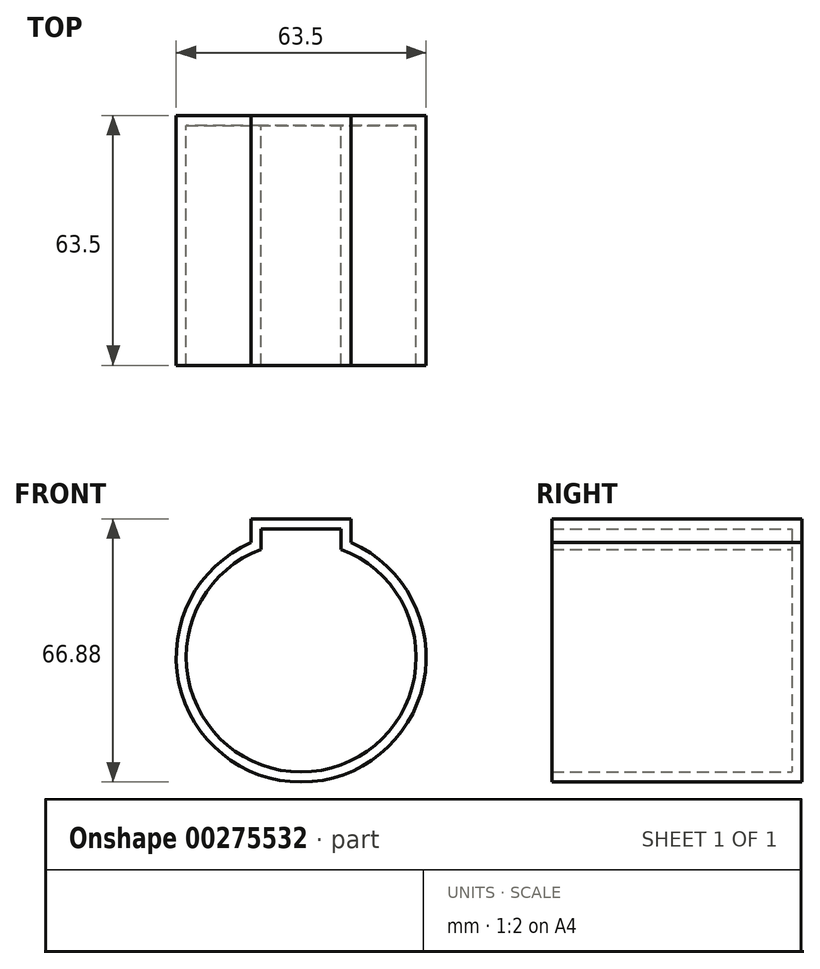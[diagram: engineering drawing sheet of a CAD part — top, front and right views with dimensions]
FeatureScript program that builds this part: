
annotation { "Feature Type Name" : "Feature", "Feature Type Description" : "" }
export const myFeature = defineFeature(function(context is Context, id is Id, definition is map)
    precondition{}
    {
        {
            var Q0;
            Q0=qCreatedBy(makeId("Front.planeOp"),FACE);
            var sketch = newSketch(context, id + "F0", { "sketchPlane" : qUnion([Q0])});
            skCircle(sketch, "E0", {"center": v(0, 0) * mm, "radius": 31.75 * mm});
            skLineSegment(sketch, "E1.bottom", {"start": v(12.7, 35.13) * mm, "end": v(-12.7, 35.13) * mm});
            skLineSegment(sketch, "E1.top", {"start": v(12.7, 28.37) * mm, "end": v(-12.7, 28.37) * mm});
            skLineSegment(sketch, "E1.left", {"start": v(12.7, 35.13) * mm, "end": v(12.7, 28.37) * mm});
            skLineSegment(sketch, "E1.right", {"start": v(-12.7, 35.13) * mm, "end": v(-12.7, 28.37) * mm});
            skPoint(sketch, "E1.middle", {"position": v(0, 31.75) * mm});
            skCircle(sketch, "E2", {"center": v(0, 0) * mm, "radius": 29.08 * mm});
            skSolve(sketch);
        }
        {
            var Q0;
            {var subQ5=sQuery(id+"F0.wireOp",EDGE,"E1.bottom");Q0=makeQuery(id+"F0.imprint","IMPRINT",FACE,{"disambiguationData":[TD([[makeQuery(id+"F0.imprint","IMPRINT",EDGE,{"derivedFrom":subQ5}),1.0]])]});}
            var Q1;
            {var subQ0=sQuery(id+"F0.wireOp",EDGE,"E1.left");var subQ3=sQuery(id+"F0.wireOp",EDGE,"E0");var subQ4=makeQuery(id+"F0.imprint","INTERSECT",VERTEX,{"derivedFrom":[subQ3,subQ0]});Q1=makeQuery(id+"F0.imprint","IMPRINT",FACE,{"disambiguationData":[TD([[makeQuery(id+"F0.imprint","IMPRINT",EDGE,{"disambiguationData":[TD([[subQ4,1.0]])],"derivedFrom":subQ3}),1.0]])]});}
            var Q2;
            {var subQ0=sQuery(id+"F0.wireOp",EDGE,"E2");var subQ1=sQuery(id+"F0.wireOp",EDGE,"E1.top");var subQ2=makeQuery(id+"F0.imprint","INTERSECT",VERTEX,{"disambiguationData":[OD(0.0)],"derivedFrom":[subQ1,subQ0]});Q2=makeQuery(id+"F0.imprint","IMPRINT",FACE,{"disambiguationData":[TD([[makeQuery(id+"F0.imprint","IMPRINT",EDGE,{"disambiguationData":[TD([[subQ2,-1.0]])],"derivedFrom":subQ1}),1.0]])]});}
            var Q3;
            {var subQ0=sQuery(id+"F0.wireOp",EDGE,"E2");var subQ1=sQuery(id+"F0.wireOp",EDGE,"E1.top");var subQ2=makeQuery(id+"F0.imprint","INTERSECT",VERTEX,{"disambiguationData":[OD(0.0)],"derivedFrom":[subQ1,subQ0]});Q3=makeQuery(id+"F0.imprint","IMPRINT",FACE,{"disambiguationData":[TD([[makeQuery(id+"F0.imprint","IMPRINT",EDGE,{"disambiguationData":[TD([[subQ2,-1.0]])],"derivedFrom":subQ1}),-1.0]])]});}
            var Q4;
            {var subQ0=sQuery(id+"F0.wireOp",EDGE,"E1.left");var subQ3=sQuery(id+"F0.wireOp",EDGE,"E0");var subQ4=makeQuery(id+"F0.imprint","INTERSECT",VERTEX,{"derivedFrom":[subQ3,subQ0]});Q4=makeQuery(id+"F0.imprint","IMPRINT",FACE,{"disambiguationData":[TD([[makeQuery(id+"F0.imprint","IMPRINT",EDGE,{"disambiguationData":[TD([[subQ4,-1.0]])],"derivedFrom":subQ3}),1.0]])]});}
            extrude(context, id + "F1", {"entities" : qUnion([Q0, Q1, Q2, Q3, Q4]), "depth" : 63.5 * mm});
        }
        {
            var Q0;
            Q0=makeQuery(id+"F1.opExtrude","CAP_FACE",FACE,{"disambiguationData":[OSD([sQuery(id+"F0.wireOp",EDGE,"E0"),sQuery(id+"F0.wireOp",EDGE,"E1.bottom"),sQuery(id+"F0.wireOp",EDGE,"E1.top"),sQuery(id+"F0.wireOp",EDGE,"E1.left"),sQuery(id+"F0.wireOp",EDGE,"E1.right"),sQuery(id+"F0.wireOp",EDGE,"E2")])],"isStart":false});
            shell(context, id + "F2", {"entities" : qUnion([Q0]), "thickness" : 2.54 * mm});
        }
    });
